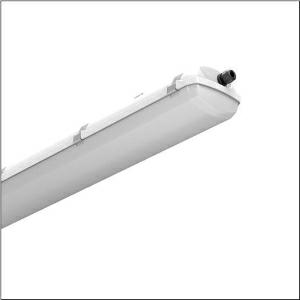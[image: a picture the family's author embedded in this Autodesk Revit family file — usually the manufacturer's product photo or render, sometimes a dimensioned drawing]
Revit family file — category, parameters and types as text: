
# Revit family: monsun_ex_51fxb17p4d0a
name_source: partatom
category: Lighting Fixtures
units: mm (PartAtom-declared; Revit-internal decimal feet)

## family parameters
Cut with Voids When Loaded = No
Host = Face
Light Source = No
Part Type = Normal
Room Calculation Point = No
Round Connector Dimension = Use Diameter
Shared = No

## types (1)
- Monsun Ex (1 x LED, 17900 lm, 116.3 W, 4000K)
    Apparent Load = 116 VA
    CIE Flux Codes = 61 86 97 98 100
    Color Rendering = 80
    Color Temperature = 4000K
    Default Elevation = 1800 mm
    Description = Monsun Ex, damp-proof luminaire, primary optical cover: cover, of PC, UV-stabilised, opal, light emission: direct distribution, primary light characteristic: symmetric, installation type: surface-mounted, LED, rated luminous flux: 17.900lm, luminous efficacy: 154lm/W, light colour: 840, colour temperature: 4000K, control gear: ON/OFF, with terminal, 3-pole, max. 2.5mm², through-wiring: 5x 2.5mm², mains connection: 220..240V, AC, 50/60Hz, rated input power: 116W, housing, of PC, light grey (RAL 7035), incl. blanking plug, incl. 2x Ex cable gland M20 for cable diameter 7..12mm with sealing, length: 1.580mm, width: 155mm, height: 105mm, clip for enclosure, of stainless steel, protection rating (complete): IP66, insulation class (complete): insulation class I (protective earthing), certification: CE, explosion class: zone2,22 II 3G Ex nR IIC T6 GC, II 3D Ex tc IIIC T80°C Dc, impact resistance: IK10, permissible operating ambient temperature: -20..+40°C, LABS conformity tested according to VDMA 24364:2018-05, contact your sales advisor before using the luminaires in applications with unclear chemical exposure, large temperature fluctuations or condensation-forming humidity, packaging unit: 1 piece
    Height = 105 mm
    Lamp = 1 x LED
    Lamp Light Flux = 17900 lm
    Lamp Power = 116.3 W
    Lamp count = 1
    Length = 1580 mm
    Luminous efficacy = 154 lm/W
    Manufacturer = Siteco
    ModVariant = No
    Model = 51FXB17P4D0A
    Mounting Place = Ceiling
    Mounting Type = Surface mounted
    Number of Poles = 1
    OnlyDefault = Yes
    Power Factor = 1
    Product Name = Monsun Ex
    Product group = damp-proof luminaire
    ProductGroupID = 300
    Protection Class = Protection class I
    Protection Degree = IP 66
    RLX_Detail_Level = 1
    RLX_Emergency_Light_Flux = 0 lm
    RLX_Emergency_Type = 0
    RLX_Emergency_Type_DB = No
    RlxData = <blob elided: 41757 chars, md5=f35485b2>
    Socket = socket
    Standby Power = 0 W
    System Light Flux = 17900 lm
    System Power = 116 W
    Type Comments = Product without accessories
    Type Image = l_1258882.jpg
    URL = http://relux.com
    VarID = ---
    Voltage = 0 V
    Weight = 0.00 kg
    Width = 155 mm

## geometry (parser evidence)
native form markers: Blend x4, Sweep x8
no freeform markers — native parametric forms only
